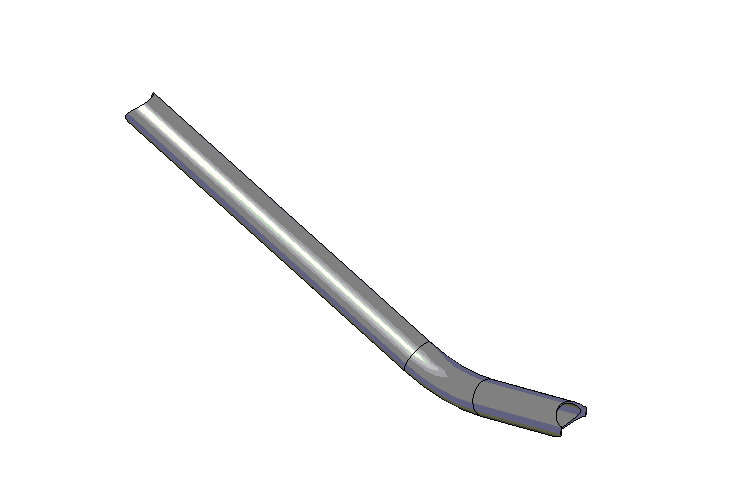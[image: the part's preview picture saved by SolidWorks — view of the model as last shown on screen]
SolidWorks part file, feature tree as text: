
SOLIDWORKS PART (.sldprt)
format: sldprt  version: not decoded by parser v0  size: 393,728 bytes
history: native  units: mm
features: plane x11, sketch x11, material x1, sweep x1, extrude x1, cut_revolve x1, cut_extrude x1 (+10 scaffold rows collapsed)
feature tree (37):
  scaffold x10  (default folders/planes/origin — collapsed)
  material  "Matériau <non spécifié>"
  plane  "Plan de face"
  plane  "Plan de dessus"
  plane  "Plan de droite"
  sketch  "Esquisse1"  dims[c1.D1=625.0mm c1.D2=460.0mm c1.D3=545.0mm c1.D4=27.0mm c1.D5=500.0mm c1.D6=445.0mm c1.D7=670.0mm c2.D1=622.0mm c2.D2=670.0mm c2.D3=545.0mm c2.D4=460.0mm c2.D5=445.0mm c2.D6=495.0mm c2.D7=535.0mm c2.D8=27.0mm c2.D9=8.0mm c2.D10=155.0mm c2.D11=400.0mm c2.D12=~545.374305mm c3.D12=56.0deg]
  plane  "Plan1"
  plane  "Plan2"  Offset=180mm
  plane  "Plan3"  Offset=340mm
  plane  "Plan4"  Offset=500mm
  plane  "Plan5"
  plane  "Plan6"
  sketch  "Esquisse10"  dims[c1.D1=30.0mm c1.D2=~323.286475mm c1.D3=~161.643237mm c2.D2=34.0mm]
  sketch  "Esquisse11"  dims[D1=130.0mm]
  plane  "Plan7"
  plane  "Plan8"
  sweep  "Balayage1"
  sketch  "Esquisse12"
  extrude  "Extrusion1"  [1 undecoded]
  sketch  "Esquisse3"  dims[c1.D1=50.0mm c1.D2=45.0mm c1.D3=~233.713088mm c2.D2=140.0mm c2.D3=45.0mm c2.D4=9.0mm c2.D5=80.0mm c2.D6=27.0mm]
  cut_revolve  "Enlèvement de matière-Révolution1"  Angle=360deg
  sketch  "Esquisse5"  dims[c1.D1=42.0mm c1.D2=55.0mm c1.D3=2.0mm c1.D4=~8.95384mm c2.D3=2.0mm c2.D4=2.0mm]
  sketch  "Esquisse6"  dims[D1=50.0mm D2=46.0mm]
  sketch  "Esquisse7"  dims[D1=46.0mm]
  sketch  "Esquisse8"
  sketch  "Esquisse9"  dims[D1=45.0mm D2=41.0mm]
  sketch  "Esquisse13"  dims[D1=32.0mm]
  cut_extrude  "Enlèv. mat.-Extru.1"  [1 undecoded]
decode coverage: 10 of 15 modeling features carry decoded parameters
note: ~ marks probable driven/reference dimensions
note: 2 parameter values undecoded
note: suppression state not decoded; provenance and decode notes live in map.json
